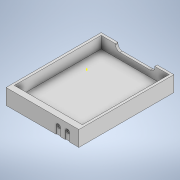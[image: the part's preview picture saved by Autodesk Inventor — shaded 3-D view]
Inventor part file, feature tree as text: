
AUTODESK INVENTOR PART (.ipt)
format: ipt  version: 2021.2 (Build 252289000, 289)  size: 530,432 bytes
history: native  units: in
note: dims shown in document units (in); Inventor stores cm internally (conversion verified against a paired STEP export)
features: sketch x37, extrude x31, fillet x1
ambient origin geometry x8: Origin, YZ Plane, XZ Plane, XY Plane, X Axis, Y Axis, Z Axis, Center Point
bodies: Solid1 (feature_tree)
feature tree (69):
  extrude  "Extrusion1"  Depth=1.315in
  extrude  "Extrusion2"  Depth=0.0433in
  extrude  "Extrusion3"  Depth=0.0433in
  extrude  "Extrusion4"  Depth=1.5669in
  sketch  "Sketch6"  dims[d11=0.1929in d12=0.0in d13=0.0236in d14=0.0in]
  extrude  "Extrusion5"  Depth=0.0236in TaperAngle=0.0deg
  extrude  "Extrusion6"  Depth=0.1181in
  sketch  "Sketch8"  dims[d18=0.0512in d19=0.1417in]
  extrude  "Extrusion7"  Depth=0.1417in
  extrude  "Extrusion8"  Depth=0.0984in TaperAngle=0.0deg
  extrude  "Extrusion9"  Depth=0.0394in
  extrude  "Extrusion10"  Depth=0.0394in
  extrude  "Extrusion11"  TaperAngle=0.0deg  [1 undecoded]
  sketch  "Sketch14"  dims[d35=0.0118in d36=0.0512in d37=0.0in]
  extrude  "Extrusion12"  Depth=0.0787in
  extrude  "Extrusion13"  TaperAngle=0.0deg  [1 undecoded]
  extrude  "Extrusion14"  Depth=0.0118in
  extrude  "Extrusion15"  Depth=0.0787in
  extrude  "Extrusion16"  Depth=0.0984in
  sketch  "Sketch20"  dims[d51=0.0512in d52=0.0394in d53=0.0591in d54=0.0591in]
  extrude  "Extrusion17"  TaperAngle=0.0deg  [1 undecoded]
  sketch  "Sketch22"  dims[d57=0.0591in d58=0.0in d59=0.0315in]
  extrude  "Extrusion18"  Depth=0.0394in
  extrude  "Extrusion19"  Depth=0.0394in
  extrude  "Extrusion20"  TaperAngle=0.0deg  [1 undecoded]
  extrude  "Extrusion21"  Depth=0.0315in
  extrude  "Extrusion22"  Depth=0.0433in
  extrude  "Extrusion23"  TaperAngle=0.0deg  [1 undecoded]
  sketch  "Sketch29"  dims[d80=0.0787in d81=0.0in d82=0.0394in]
  extrude  "Extrusion24"  Depth=0.0433in TaperAngle=0.0deg
  extrude  "Extrusion25"  TaperAngle=0.0deg  [1 undecoded]
  extrude  "Extrusion26"  Depth=0.0079in
  extrude  "Extrusion27"  Depth=0.0433in TaperAngle=0.0deg
  extrude  "Extrusion28"  Depth=0.0394in
  extrude  "Extrusion29"  Depth=0.0787in
  fillet  "Fillet1"  Radius=0.0394in
  extrude  "Extrusion30"  Depth=0.0984in TaperAngle=0.0deg
  sketch  "Sketch36"  dims[d94=0.0787in]
  sketch  "Sketch37"  dims[d95=0.0039in d96=0.0in]
  extrude  "Extrusion31"  Depth=0.0787in
  sketch  "Sketch2"  dims[d2=1.6535in d3=1.315in]
  sketch  "Sketch3"  dims[d4=0.2362in d5=0.0in d6=0.0433in]
  sketch  "Sketch4"  dims[d7=0.0433in d8=0.0433in]
  sketch  "Sketch5"  dims[d9=0.0433in d10=1.5669in]
  sketch  "Sketch7"  dims[d15=0.1181in d16=0.0in d17=0.1181in]
  sketch  "Sketch9"  dims[d20=0.0394in d21=0.0984in d22=0.0in]
  sketch  "Sketch10"  dims[d23=0.1181in d24=0.0512in d25=0.1181in d26=0.0512in d27=0.0394in]
  sketch  "Sketch11"  dims[d28=0.0394in d29=0.0276in]
  sketch  "Sketch12"  dims[d30=0.0276in d31=0.0in d32=0.0in]
  sketch  "Sketch13"  dims[d33=0.0118in d34=0.0787in]
  sketch  "Sketch15"  dims[d38=0.0792in d39=0.0118in d40=0.0512in]
  sketch  "Sketch16"  dims[d41=0.0in d42=0.0787in]
  sketch  "Sketch17"  dims[d43=0.0984in d44=0.0in d45=0.0512in]
  sketch  "Sketch18"  dims[d46=0.0394in d47=0.0in]
  sketch  "Sketch19"  dims[d48=0.0591in d49=0.0512in d50=0.0394in]
  sketch  "Sketch21"  dims[d55=0.0in d56=0.0in]
  sketch  "Sketch23"  dims[d60=0.0591in d61=0.0in d62=0.0433in]
  sketch  "Sketch24"  dims[d63=0.0in d64=0.0in d65=0.0in d66=0.0in]
  sketch  "Sketch25"  dims[d67=0.0433in d68=0.0in d69=0.0433in d70=0.0in]
  sketch  "Sketch26"  dims[d71=0.0433in d72=0.0in d73=0.0in]
  sketch  "Sketch27"  dims[d74=0.0079in d75=0.0079in]
  sketch  "Sketch28"  dims[d76=0.0433in d77=0.0in d78=0.0433in d79=0.0in]
  sketch  "Sketch30"  dims[d83=0.0787in d84=0.0787in d85=0.0394in]
  sketch  "Sketch31"  dims[d86=0.0295in d87=0.0984in d88=0.0in]
  sketch  "Sketch32"  dims[d89=0.0295in d90=0.0787in]
  sketch  "Sketch33"  dims[d91=0.0394in]
  sketch  "Sketch34"  dims[d92=0.0295in]
  sketch  "Sketch35"  dims[d93=0.0394in]
  sketch  "Sketch38"  dims[d97=0.0984in d98=0.0in d99=0.0591in d100=0.0591in d101=0.0984in d102=0.0in d103=0.0039in d104=0.0in d105=0.0079in d106=0.0in d107=0.0079in d108=0.0in d109=0.0079in d110=0.0in d111=0.1181in d112=0.0in d113=0.0394in d114=0.0in d115=0.0197in d116=0.0in d117=0.7087in d118=0.3031in d119=0.0984in d120=0.0472in d121=0.0in d122=0.0787in d123=0.0118in d124=0.0in d125=0.0787in d126=0.0236in d127=0.0in]
note: 6 required parameter values undecoded (feature->parameter linkage not recoverable at this tier; creation-order binding heuristic only, values carry confidence <= 0.55)
